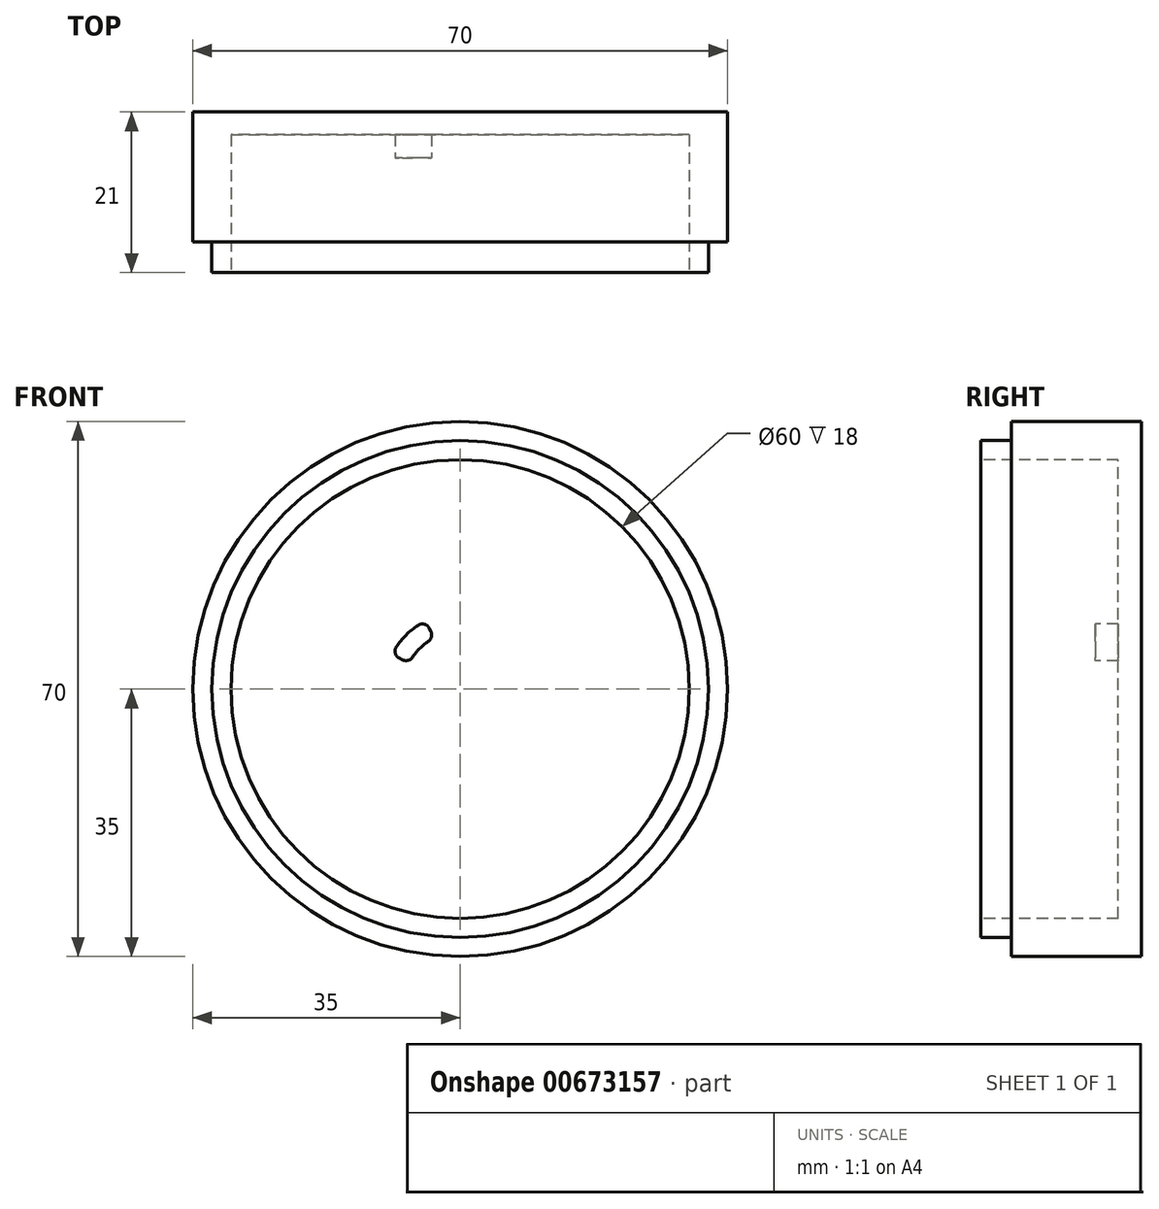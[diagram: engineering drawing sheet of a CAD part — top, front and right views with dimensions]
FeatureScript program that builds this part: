
annotation { "Feature Type Name" : "Feature", "Feature Type Description" : "" }
export const myFeature = defineFeature(function(context is Context, id is Id, definition is map)
    precondition{}
    {
        {
            var Q0;
            Q0=qCreatedBy(makeId("Front.planeOp"),FACE);
            var sketch = newSketch(context, id + "F0", { "sketchPlane" : qUnion([Q0])});
            skCircle(sketch, "E0", {"center": v(0, 0) * mm, "radius": 35 * mm});
            skSolve(sketch);
        }
        {
            var Q0;
            Q0=makeQuery(id+"F0.imprint","IMPRINT",FACE,{"disambiguationData":[TD([[makeQuery(id+"F0.imprint","IMPRINT",EDGE,{"derivedFrom":sQuery(id+"F0.wireOp",EDGE,"E0")}),1.0]])]});
            extrude(context, id + "F1", {"entities" : qUnion([Q0]), "depth" : 21 * mm, "offsetDistance" : 25 * mm});
        }
        {
            var Q0;
            Q0=makeQuery(id+"F1.opExtrude","CAP_FACE",FACE,{"disambiguationData":[OSD([sQuery(id+"F0.wireOp",EDGE,"E0")])],"isStart":false});
            var sketch = newSketch(context, id + "F2", { "sketchPlane" : qUnion([Q0])});
            skCircle(sketch, "E1", {"center": v(0, 0) * mm, "radius": 30 * mm});
            skSolve(sketch);
        }
        {
            var Q0;
            Q0=makeQuery(id+"F2.imprint","IMPRINT",FACE,{"disambiguationData":[TD([[makeQuery(id+"F2.imprint","IMPRINT",EDGE,{"derivedFrom":sQuery(id+"F2.wireOp",EDGE,"E1")}),1.0]])]});
            extrude(context, id + "F3", {"entities" : qUnion([Q0]), "operationType" : NewBodyOperationType.REMOVE, "oppositeDirection" : true, "depth" : 15 * mm, "offsetDistance" : 25 * mm});
        }
        {
            var Q0;
            Q0=makeQuery(id+"F1.opExtrude","CAP_FACE",FACE,{"disambiguationData":[OSD([sQuery(id+"F0.wireOp",EDGE,"E0")])],"isStart":false});
            var sketch = newSketch(context, id + "F4", { "sketchPlane" : qUnion([Q0])});
            skCircle(sketch, "E2", {"center": v(0, 0) * mm, "radius": 32.5 * mm});
            skSolve(sketch);
        }
        {
            var Q0;
            Q0=makeQuery(id+"F4.imprint","IMPRINT",FACE,{"disambiguationData":[TD([[makeQuery(id+"F4.imprint","IMPRINT",EDGE,{"derivedFrom":sQuery(id+"F4.wireOp",EDGE,"E2")}),-1.0]])]});
            extrude(context, id + "F5", {"entities" : qUnion([Q0]), "operationType" : NewBodyOperationType.REMOVE, "oppositeDirection" : true, "depth" : 4 * mm, "offsetDistance" : 25 * mm});
        }
        {
            var Q0;
            Q0=makeQuery(id+"F3.boolean.opBoolean","COPY",FACE,{"derivedFrom":makeQuery(id+"F3.opExtrude","CAP_FACE",FACE,{"disambiguationData":[OSD([sQuery(id+"F2.wireOp",EDGE,"E1")])],"isStart":false})});
            var sketch = newSketch(context, id + "F6", { "sketchPlane" : qUnion([Q0])});
            skLineSegment(sketch, "E3", {"start": v(0, 0) * mm, "end": v(0, 30) * mm, "construction": true});
            skLineSegment(sketch, "E4", {"start": v(-30, 0) * mm, "end": v(0, 0) * mm, "construction": true});
            skLineSegment(sketch, "E5", {"start": v(-2, 4) * mm, "end": v(-2, 25) * mm});
            skLineSegment(sketch, "E6", {"start": v(0, 27) * mm, "end": v(0, 27) * mm});
            skPoint(sketch, "E7.visualSharp", {"position": v(-2, 27) * mm});
            skArc(sketch, "E7.filletArc", {"start": v(0, 27) * mm, "mid": v(-1.41, 26.41) * mm, "end": v(-2, 25) * mm});
            skArc(sketch, "E8.MirrorCS", {"start": v(0, 27) * mm, "mid": v(1.41, 26.41) * mm, "end": v(2, 25) * mm});
            skLineSegment(sketch, "E9.MirrorCS", {"start": v(2, 4) * mm, "end": v(2, 25) * mm});
            skPoint(sketch, "E10.1.0", {"position": v(-27, -2) * mm});
            skLineSegment(sketch, "E10.1.1", {"start": v(-4, -2) * mm, "end": v(-25, -2) * mm});
            skLineSegment(sketch, "E10.1.2", {"start": v(-4, 2) * mm, "end": v(-25, 2) * mm});
            skArc(sketch, "E10.1.3", {"start": v(-27, 0) * mm, "mid": v(-26.41, -1.41) * mm, "end": v(-25, -2) * mm});
            skArc(sketch, "E10.1.4", {"start": v(-27, 0) * mm, "mid": v(-26.41, 1.41) * mm, "end": v(-25, 2) * mm});
            skPoint(sketch, "E10.2.0", {"position": v(2, -27) * mm});
            skLineSegment(sketch, "E10.2.1", {"start": v(2, -4) * mm, "end": v(2, -25) * mm});
            skLineSegment(sketch, "E10.2.2", {"start": v(-2, -4) * mm, "end": v(-2, -25) * mm});
            skArc(sketch, "E10.2.3", {"start": v(0, -27) * mm, "mid": v(1.41, -26.41) * mm, "end": v(2, -25) * mm});
            skArc(sketch, "E10.2.4", {"start": v(0, -27) * mm, "mid": v(-1.41, -26.41) * mm, "end": v(-2, -25) * mm});
            skPoint(sketch, "E10.3.0", {"position": v(27, 2) * mm});
            skLineSegment(sketch, "E10.3.1", {"start": v(4, 2) * mm, "end": v(25, 2) * mm});
            skLineSegment(sketch, "E10.3.2", {"start": v(4, -2) * mm, "end": v(25, -2) * mm});
            skArc(sketch, "E10.3.3", {"start": v(27, 0) * mm, "mid": v(26.41, 1.41) * mm, "end": v(25, 2) * mm});
            skArc(sketch, "E10.3.4", {"start": v(27, 0) * mm, "mid": v(26.41, -1.41) * mm, "end": v(25, -2) * mm});
            skPoint(sketch, "E10.center", {"position": v(0, 0) * mm});
            skPoint(sketch, "E11.orphan", {"position": v(0, 2) * mm});
            skPoint(sketch, "E12.orphan", {"position": v(0, -2) * mm});
            skPoint(sketch, "E13.orphan", {"position": v(-2, 0) * mm});
            skPoint(sketch, "E14.orphan", {"position": v(2, 0) * mm});
            skPoint(sketch, "E15.visualSharp", {"position": v(-2, 2) * mm});
            skArc(sketch, "E15.filletArc", {"start": v(-4, 2) * mm, "mid": v(-2.59, 2.59) * mm, "end": v(-2, 4) * mm});
            skPoint(sketch, "E16.visualSharp", {"position": v(2, 2) * mm});
            skArc(sketch, "E16.filletArc", {"start": v(2, 4) * mm, "mid": v(2.59, 2.59) * mm, "end": v(4, 2) * mm});
            skPoint(sketch, "E17.visualSharp", {"position": v(-2, -2) * mm});
            skArc(sketch, "E17.filletArc", {"start": v(-2, -4) * mm, "mid": v(-2.59, -2.59) * mm, "end": v(-4, -2) * mm});
            skPoint(sketch, "E18.visualSharp", {"position": v(2, -2) * mm});
            skArc(sketch, "E18.filletArc", {"start": v(4, -2) * mm, "mid": v(2.59, -2.59) * mm, "end": v(2, -4) * mm});
            skSolve(sketch);
        }
        {
            var Q0;
            Q0=makeQuery(id+"F6.imprint","IMPRINT",FACE,{"disambiguationData":[TD([[makeQuery(id+"F6.imprint","IMPRINT",EDGE,{"derivedFrom":sQuery(id+"F6.wireOp",EDGE,"E5")}),-1.0]])]});
            extrude(context, id + "F7", {"entities" : qUnion([Q0]), "operationType" : NewBodyOperationType.REMOVE, "oppositeDirection" : true, "depth" : 3 * mm, "offsetDistance" : 25 * mm});
        }
        {
            var Q0;
            Q0=makeQuery(id+"F3.boolean.opBoolean","COPY",FACE,{"derivedFrom":makeQuery(id+"F3.opExtrude","CAP_FACE",FACE,{"disambiguationData":[OSD([sQuery(id+"F2.wireOp",EDGE,"E1")])],"isStart":false})});
            var sketch = newSketch(context, id + "F8", { "sketchPlane" : qUnion([Q0])});
            skLineSegment(sketch, "E19", {"start": v(0, 0) * mm, "end": v(-21.21, 21.21) * mm, "construction": true});
            skArc(sketch, "E20", {"start": v(-5.3, 5.3) * mm, "mid": v(-4.75, 5.8) * mm, "end": v(-4.16, 6.24) * mm});
            skLineSegment(sketch, "E21", {"start": v(-3.82, 7.53) * mm, "end": v(-4.05, 7.98) * mm});
            skArc(sketch, "E22", {"start": v(-7.07, 7.07) * mm, "mid": v(-6.31, 7.76) * mm, "end": v(-5.49, 8.36) * mm});
            skArc(sketch, "E23.filletArc", {"start": v(-4.05, 7.98) * mm, "mid": v(-4.68, 8.49) * mm, "end": v(-5.49, 8.36) * mm});
            skArc(sketch, "E24.filletArc", {"start": v(-4.16, 6.24) * mm, "mid": v(-3.75, 6.82) * mm, "end": v(-3.82, 7.53) * mm});
            skArc(sketch, "E25.MirrorCS", {"start": v(-7.07, 7.07) * mm, "mid": v(-7.76, 6.31) * mm, "end": v(-8.36, 5.49) * mm});
            skArc(sketch, "E26.MirrorCS", {"start": v(-7.98, 4.05) * mm, "mid": v(-8.49, 4.68) * mm, "end": v(-8.36, 5.49) * mm});
            skArc(sketch, "E27.MirrorCS", {"start": v(-6.24, 4.16) * mm, "mid": v(-6.82, 3.75) * mm, "end": v(-7.53, 3.82) * mm});
            skArc(sketch, "E28.MirrorCS", {"start": v(-5.3, 5.3) * mm, "mid": v(-5.8, 4.75) * mm, "end": v(-6.24, 4.16) * mm});
            skLineSegment(sketch, "E29.MirrorCS", {"start": v(-7.53, 3.82) * mm, "end": v(-7.98, 4.05) * mm});
            skLineSegment(sketch, "E30.1.0", {"start": v(-7.53, -3.82) * mm, "end": v(-7.98, -4.05) * mm});
            skLineSegment(sketch, "E30.1.1", {"start": v(-3.82, -7.53) * mm, "end": v(-4.05, -7.98) * mm});
            skArc(sketch, "E30.1.2", {"start": v(-5.3, -5.3) * mm, "mid": v(-4.75, -5.8) * mm, "end": v(-4.16, -6.24) * mm});
            skArc(sketch, "E30.1.3", {"start": v(-4.16, -6.24) * mm, "mid": v(-3.75, -6.82) * mm, "end": v(-3.82, -7.53) * mm});
            skArc(sketch, "E30.1.4", {"start": v(-4.05, -7.98) * mm, "mid": v(-4.68, -8.49) * mm, "end": v(-5.49, -8.36) * mm});
            skArc(sketch, "E30.1.5", {"start": v(-7.07, -7.07) * mm, "mid": v(-6.31, -7.76) * mm, "end": v(-5.49, -8.36) * mm});
            skArc(sketch, "E30.1.6", {"start": v(-7.07, -7.07) * mm, "mid": v(-7.76, -6.31) * mm, "end": v(-8.36, -5.49) * mm});
            skArc(sketch, "E30.1.7", {"start": v(-5.3, -5.3) * mm, "mid": v(-5.8, -4.75) * mm, "end": v(-6.24, -4.16) * mm});
            skArc(sketch, "E30.1.8", {"start": v(-6.24, -4.16) * mm, "mid": v(-6.82, -3.75) * mm, "end": v(-7.53, -3.82) * mm});
            skArc(sketch, "E30.1.9", {"start": v(-7.98, -4.05) * mm, "mid": v(-8.49, -4.68) * mm, "end": v(-8.36, -5.49) * mm});
            skLineSegment(sketch, "E30.2.0", {"start": v(3.82, -7.53) * mm, "end": v(4.05, -7.98) * mm});
            skLineSegment(sketch, "E30.2.1", {"start": v(7.53, -3.82) * mm, "end": v(7.98, -4.05) * mm});
            skArc(sketch, "E30.2.2", {"start": v(5.3, -5.3) * mm, "mid": v(5.8, -4.75) * mm, "end": v(6.24, -4.16) * mm});
            skArc(sketch, "E30.2.3", {"start": v(6.24, -4.16) * mm, "mid": v(6.82, -3.75) * mm, "end": v(7.53, -3.82) * mm});
            skArc(sketch, "E30.2.4", {"start": v(7.98, -4.05) * mm, "mid": v(8.49, -4.68) * mm, "end": v(8.36, -5.49) * mm});
            skArc(sketch, "E30.2.5", {"start": v(7.07, -7.07) * mm, "mid": v(7.76, -6.31) * mm, "end": v(8.36, -5.49) * mm});
            skArc(sketch, "E30.2.6", {"start": v(7.07, -7.07) * mm, "mid": v(6.31, -7.76) * mm, "end": v(5.49, -8.36) * mm});
            skArc(sketch, "E30.2.7", {"start": v(5.3, -5.3) * mm, "mid": v(4.75, -5.8) * mm, "end": v(4.16, -6.24) * mm});
            skArc(sketch, "E30.2.8", {"start": v(4.16, -6.24) * mm, "mid": v(3.75, -6.82) * mm, "end": v(3.82, -7.53) * mm});
            skArc(sketch, "E30.2.9", {"start": v(4.05, -7.98) * mm, "mid": v(4.68, -8.49) * mm, "end": v(5.49, -8.36) * mm});
            skLineSegment(sketch, "E30.3.0", {"start": v(7.53, 3.82) * mm, "end": v(7.98, 4.05) * mm});
            skLineSegment(sketch, "E30.3.1", {"start": v(3.82, 7.53) * mm, "end": v(4.05, 7.98) * mm});
            skArc(sketch, "E30.3.2", {"start": v(5.3, 5.3) * mm, "mid": v(4.75, 5.8) * mm, "end": v(4.16, 6.24) * mm});
            skArc(sketch, "E30.3.3", {"start": v(4.16, 6.24) * mm, "mid": v(3.75, 6.82) * mm, "end": v(3.82, 7.53) * mm});
            skArc(sketch, "E30.3.4", {"start": v(4.05, 7.98) * mm, "mid": v(4.68, 8.49) * mm, "end": v(5.49, 8.36) * mm});
            skArc(sketch, "E30.3.5", {"start": v(7.07, 7.07) * mm, "mid": v(6.31, 7.76) * mm, "end": v(5.49, 8.36) * mm});
            skArc(sketch, "E30.3.6", {"start": v(7.07, 7.07) * mm, "mid": v(7.76, 6.31) * mm, "end": v(8.36, 5.49) * mm});
            skArc(sketch, "E30.3.7", {"start": v(5.3, 5.3) * mm, "mid": v(5.8, 4.75) * mm, "end": v(6.24, 4.16) * mm});
            skArc(sketch, "E30.3.8", {"start": v(6.24, 4.16) * mm, "mid": v(6.82, 3.75) * mm, "end": v(7.53, 3.82) * mm});
            skArc(sketch, "E30.3.9", {"start": v(7.98, 4.05) * mm, "mid": v(8.49, 4.68) * mm, "end": v(8.36, 5.49) * mm});
            skSolve(sketch);
        }
        {
            var Q0;
            Q0=makeQuery(id+"F8.imprint","IMPRINT",FACE,{"disambiguationData":[TD([[makeQuery(id+"F8.imprint","IMPRINT",EDGE,{"derivedFrom":sQuery(id+"F8.wireOp",EDGE,"E20")}),1.0]])]});
            var Q1;
            Q1=makeQuery(id+"F8.imprint","IMPRINT",FACE,{"disambiguationData":[TD([[makeQuery(id+"F8.imprint","IMPRINT",EDGE,{"derivedFrom":sQuery(id+"F8.wireOp",EDGE,"E30.3.0")}),1.0]])]});
            var Q2;
            Q2=makeQuery(id+"F8.imprint","IMPRINT",FACE,{"disambiguationData":[TD([[makeQuery(id+"F8.imprint","IMPRINT",EDGE,{"derivedFrom":sQuery(id+"F8.wireOp",EDGE,"E30.2.0")}),1.0]])]});
            var Q3;
            Q3=makeQuery(id+"F8.imprint","IMPRINT",FACE,{"disambiguationData":[TD([[makeQuery(id+"F8.imprint","IMPRINT",EDGE,{"derivedFrom":sQuery(id+"F8.wireOp",EDGE,"E30.1.0")}),1.0]])]});
            extrude(context, id + "F9", {"entities" : qUnion([Q0, Q1, Q2, Q3]), "operationType" : NewBodyOperationType.REMOVE, "oppositeDirection" : true, "depth" : 3 * mm, "offsetDistance" : 25 * mm});
        }
        {
            var Q0;
            Q0=makeQuery(id+"F3.boolean.opBoolean","COPY",FACE,{"derivedFrom":makeQuery(id+"F3.opExtrude","CAP_FACE",FACE,{"disambiguationData":[OSD([sQuery(id+"F2.wireOp",EDGE,"E1")])],"isStart":false})});
            var sketch = newSketch(context, id + "F10", { "sketchPlane" : qUnion([Q0])});
            skLineSegment(sketch, "E31", {"start": v(-9.93, 11.83) * mm, "end": v(-10.58, 12.6) * mm});
            skLineSegment(sketch, "E32", {"start": v(-3.82, 14.06) * mm, "end": v(-3.82, 15.06) * mm});
            skArc(sketch, "E33", {"start": v(-9.04, 10.77) * mm, "mid": v(-10.1, 9.8) * mm, "end": v(-11.04, 8.71) * mm, "construction": true});
            skArc(sketch, "E34", {"start": v(-8, 11.51) * mm, "mid": v(-6.6, 12.19) * mm, "end": v(-5.09, 12.58) * mm});
            skArc(sketch, "E35", {"start": v(-10.22, 14.84) * mm, "mid": v(-7.96, 15.94) * mm, "end": v(-5.53, 16.55) * mm});
            skArc(sketch, "E36.filletArc", {"start": v(-3.82, 15.06) * mm, "mid": v(-4.34, 16.2) * mm, "end": v(-5.53, 16.55) * mm});
            skPoint(sketch, "E37.newPointA", {"position": v(-3.82, 0) * mm});
            skArc(sketch, "E37.filletArc", {"start": v(-5.09, 12.58) * mm, "mid": v(-4.18, 13.08) * mm, "end": v(-3.82, 14.06) * mm});
            skArc(sketch, "E38.filletArc", {"start": v(-10.22, 14.84) * mm, "mid": v(-10.9, 13.8) * mm, "end": v(-10.58, 12.6) * mm});
            skArc(sketch, "E39.filletArc", {"start": v(-9.93, 11.83) * mm, "mid": v(-9.03, 11.32) * mm, "end": v(-8, 11.51) * mm});
            skLineSegment(sketch, "E40", {"start": v(-3.82, 4.55) * mm, "end": v(0, 0) * mm, "construction": true});
            skLineSegment(sketch, "E41", {"start": v(0, 0) * mm, "end": v(-21.21, 21.21) * mm, "construction": true});
            skArc(sketch, "E42.MirrorCS", {"start": v(-15.06, 3.82) * mm, "mid": v(-16.2, 4.34) * mm, "end": v(-16.55, 5.53) * mm});
            skLineSegment(sketch, "E43.MirrorCS", {"start": v(-14.06, 3.82) * mm, "end": v(-15.06, 3.82) * mm});
            skArc(sketch, "E44.MirrorCS", {"start": v(-12.58, 5.09) * mm, "mid": v(-13.08, 4.18) * mm, "end": v(-14.06, 3.82) * mm});
            skArc(sketch, "E45.MirrorCS", {"start": v(-11.51, 8) * mm, "mid": v(-12.19, 6.6) * mm, "end": v(-12.58, 5.09) * mm});
            skArc(sketch, "E46.MirrorCS", {"start": v(-11.83, 9.93) * mm, "mid": v(-11.32, 9.03) * mm, "end": v(-11.51, 8) * mm});
            skLineSegment(sketch, "E47.MirrorCS", {"start": v(-11.83, 9.93) * mm, "end": v(-12.6, 10.58) * mm});
            skArc(sketch, "E48.MirrorCS", {"start": v(-14.84, 10.22) * mm, "mid": v(-13.8, 10.9) * mm, "end": v(-12.6, 10.58) * mm});
            skArc(sketch, "E49.MirrorCS", {"start": v(-14.84, 10.22) * mm, "mid": v(-15.94, 7.96) * mm, "end": v(-16.55, 5.53) * mm});
            skLineSegment(sketch, "E50", {"start": v(0, 0) * mm, "end": v(-30, 0) * mm, "construction": true});
            skLineSegment(sketch, "E51.MirrorCS", {"start": v(-9.93, -11.83) * mm, "end": v(-10.58, -12.6) * mm});
            skLineSegment(sketch, "E52.MirrorCS", {"start": v(-3.82, -14.06) * mm, "end": v(-3.82, -15.06) * mm});
            skLineSegment(sketch, "E53.MirrorCS", {"start": v(-11.83, -9.93) * mm, "end": v(-12.6, -10.58) * mm});
            skLineSegment(sketch, "E54.MirrorCS", {"start": v(-14.06, -3.82) * mm, "end": v(-15.06, -3.82) * mm});
            skArc(sketch, "E55.MirrorCS", {"start": v(-11.51, -8) * mm, "mid": v(-12.19, -6.6) * mm, "end": v(-12.58, -5.09) * mm});
            skArc(sketch, "E56.MirrorCS", {"start": v(-11.83, -9.93) * mm, "mid": v(-11.32, -9.03) * mm, "end": v(-11.51, -8) * mm});
            skArc(sketch, "E57.MirrorCS", {"start": v(-12.58, -5.09) * mm, "mid": v(-13.08, -4.18) * mm, "end": v(-14.06, -3.82) * mm});
            skArc(sketch, "E58.MirrorCS", {"start": v(-15.06, -3.82) * mm, "mid": v(-16.2, -4.34) * mm, "end": v(-16.55, -5.53) * mm});
            skArc(sketch, "E59.MirrorCS", {"start": v(-14.84, -10.22) * mm, "mid": v(-13.8, -10.9) * mm, "end": v(-12.6, -10.58) * mm});
            skArc(sketch, "E60.MirrorCS", {"start": v(-5.09, -12.58) * mm, "mid": v(-4.18, -13.08) * mm, "end": v(-3.82, -14.06) * mm});
            skArc(sketch, "E61.MirrorCS", {"start": v(-10.22, -14.84) * mm, "mid": v(-10.9, -13.8) * mm, "end": v(-10.58, -12.6) * mm});
            skArc(sketch, "E62.MirrorCS", {"start": v(-9.93, -11.83) * mm, "mid": v(-9.03, -11.32) * mm, "end": v(-8, -11.51) * mm});
            skArc(sketch, "E63.MirrorCS", {"start": v(-9.04, -10.77) * mm, "mid": v(-10.1, -9.8) * mm, "end": v(-11.04, -8.71) * mm, "construction": true});
            skArc(sketch, "E64.MirrorCS", {"start": v(-8, -11.51) * mm, "mid": v(-6.6, -12.19) * mm, "end": v(-5.09, -12.58) * mm});
            skArc(sketch, "E65.MirrorCS", {"start": v(-14.84, -10.22) * mm, "mid": v(-15.94, -7.96) * mm, "end": v(-16.55, -5.53) * mm});
            skArc(sketch, "E66.MirrorCS", {"start": v(-3.82, -15.06) * mm, "mid": v(-4.34, -16.2) * mm, "end": v(-5.53, -16.55) * mm});
            skArc(sketch, "E67.MirrorCS", {"start": v(-10.22, -14.84) * mm, "mid": v(-7.96, -15.94) * mm, "end": v(-5.53, -16.55) * mm});
            skLineSegment(sketch, "E68", {"start": v(0, 0) * mm, "end": v(0, 27) * mm, "construction": true});
            skLineSegment(sketch, "E69.MirrorCS", {"start": v(9.93, -11.83) * mm, "end": v(10.58, -12.6) * mm});
            skArc(sketch, "E70.MirrorCS", {"start": v(9.93, -11.83) * mm, "mid": v(9.03, -11.32) * mm, "end": v(8, -11.51) * mm});
            skLineSegment(sketch, "E71.MirrorCS", {"start": v(3.82, -14.06) * mm, "end": v(3.82, -15.06) * mm});
            skArc(sketch, "E72.MirrorCS", {"start": v(11.83, -9.93) * mm, "mid": v(11.32, -9.03) * mm, "end": v(11.51, -8) * mm});
            skLineSegment(sketch, "E73.MirrorCS", {"start": v(11.83, 9.93) * mm, "end": v(12.6, 10.58) * mm});
            skLineSegment(sketch, "E74.MirrorCS", {"start": v(11.83, -9.93) * mm, "end": v(12.6, -10.58) * mm});
            skLineSegment(sketch, "E75.MirrorCS", {"start": v(14.06, 3.82) * mm, "end": v(15.06, 3.82) * mm});
            skLineSegment(sketch, "E76.MirrorCS", {"start": v(14.06, -3.82) * mm, "end": v(15.06, -3.82) * mm});
            skArc(sketch, "E77.MirrorCS", {"start": v(9.93, 11.83) * mm, "mid": v(9.03, 11.32) * mm, "end": v(8, 11.51) * mm});
            skArc(sketch, "E78.MirrorCS", {"start": v(11.83, 9.93) * mm, "mid": v(11.32, 9.03) * mm, "end": v(11.51, 8) * mm});
            skLineSegment(sketch, "E79.MirrorCS", {"start": v(3.82, 14.06) * mm, "end": v(3.82, 15.06) * mm});
            skLineSegment(sketch, "E80.MirrorCS", {"start": v(9.93, 11.83) * mm, "end": v(10.58, 12.6) * mm});
            skArc(sketch, "E81.MirrorCS", {"start": v(12.58, 5.09) * mm, "mid": v(13.08, 4.18) * mm, "end": v(14.06, 3.82) * mm});
            skArc(sketch, "E82.MirrorCS", {"start": v(5.09, -12.58) * mm, "mid": v(4.18, -13.08) * mm, "end": v(3.82, -14.06) * mm});
            skArc(sketch, "E83.MirrorCS", {"start": v(10.22, -14.84) * mm, "mid": v(10.9, -13.8) * mm, "end": v(10.58, -12.6) * mm});
            skArc(sketch, "E84.MirrorCS", {"start": v(8, -11.51) * mm, "mid": v(6.6, -12.19) * mm, "end": v(5.09, -12.58) * mm});
            skArc(sketch, "E85.MirrorCS", {"start": v(10.22, 14.84) * mm, "mid": v(10.9, 13.8) * mm, "end": v(10.58, 12.6) * mm});
            skArc(sketch, "E86.MirrorCS", {"start": v(12.58, -5.09) * mm, "mid": v(13.08, -4.18) * mm, "end": v(14.06, -3.82) * mm});
            skArc(sketch, "E87.MirrorCS", {"start": v(15.06, -3.82) * mm, "mid": v(16.2, -4.34) * mm, "end": v(16.55, -5.53) * mm});
            skArc(sketch, "E88.MirrorCS", {"start": v(10.22, -14.84) * mm, "mid": v(7.96, -15.94) * mm, "end": v(5.53, -16.55) * mm});
            skArc(sketch, "E89.MirrorCS", {"start": v(9.04, -10.77) * mm, "mid": v(10.1, -9.8) * mm, "end": v(11.04, -8.71) * mm, "construction": true});
            skArc(sketch, "E90.MirrorCS", {"start": v(3.82, -15.06) * mm, "mid": v(4.34, -16.2) * mm, "end": v(5.53, -16.55) * mm});
            skArc(sketch, "E91.MirrorCS", {"start": v(15.06, 3.82) * mm, "mid": v(16.2, 4.34) * mm, "end": v(16.55, 5.53) * mm});
            skArc(sketch, "E92.MirrorCS", {"start": v(14.84, -10.22) * mm, "mid": v(13.8, -10.9) * mm, "end": v(12.6, -10.58) * mm});
            skArc(sketch, "E93.MirrorCS", {"start": v(14.84, 10.22) * mm, "mid": v(13.8, 10.9) * mm, "end": v(12.6, 10.58) * mm});
            skArc(sketch, "E94.MirrorCS", {"start": v(5.09, 12.58) * mm, "mid": v(4.18, 13.08) * mm, "end": v(3.82, 14.06) * mm});
            skArc(sketch, "E95.MirrorCS", {"start": v(9.04, 10.77) * mm, "mid": v(10.1, 9.8) * mm, "end": v(11.04, 8.71) * mm, "construction": true});
            skArc(sketch, "E96.MirrorCS", {"start": v(14.84, 10.22) * mm, "mid": v(15.94, 7.96) * mm, "end": v(16.55, 5.53) * mm});
            skArc(sketch, "E97.MirrorCS", {"start": v(14.84, -10.22) * mm, "mid": v(15.94, -7.96) * mm, "end": v(16.55, -5.53) * mm});
            skArc(sketch, "E98.MirrorCS", {"start": v(8, 11.51) * mm, "mid": v(6.6, 12.19) * mm, "end": v(5.09, 12.58) * mm});
            skArc(sketch, "E99.MirrorCS", {"start": v(11.51, -8) * mm, "mid": v(12.19, -6.6) * mm, "end": v(12.58, -5.09) * mm});
            skArc(sketch, "E100.MirrorCS", {"start": v(11.51, 8) * mm, "mid": v(12.19, 6.6) * mm, "end": v(12.58, 5.09) * mm});
            skPoint(sketch, "E101.MirrorP", {"position": v(3.82, 0) * mm});
            skArc(sketch, "E102.MirrorCS", {"start": v(3.82, 15.06) * mm, "mid": v(4.34, 16.2) * mm, "end": v(5.53, 16.55) * mm});
            skArc(sketch, "E103.MirrorCS", {"start": v(10.22, 14.84) * mm, "mid": v(7.96, 15.94) * mm, "end": v(5.53, 16.55) * mm});
            skSolve(sketch);
        }
        {
            var Q0;
            Q0=makeQuery(id+"F10.imprint","IMPRINT",FACE,{"disambiguationData":[TD([[makeQuery(id+"F10.imprint","IMPRINT",EDGE,{"derivedFrom":sQuery(id+"F10.wireOp",EDGE,"E31")}),-1.0]])]});
            var Q1;
            Q1=makeQuery(id+"F10.imprint","IMPRINT",FACE,{"disambiguationData":[TD([[makeQuery(id+"F10.imprint","IMPRINT",EDGE,{"derivedFrom":sQuery(id+"F10.wireOp",EDGE,"E42.MirrorCS")}),-1.0]])]});
            var Q2;
            Q2=makeQuery(id+"F10.imprint","IMPRINT",FACE,{"disambiguationData":[TD([[makeQuery(id+"F10.imprint","IMPRINT",EDGE,{"derivedFrom":sQuery(id+"F10.wireOp",EDGE,"E53.MirrorCS")}),-1.0]])]});
            var Q3;
            Q3=makeQuery(id+"F10.imprint","IMPRINT",FACE,{"disambiguationData":[TD([[makeQuery(id+"F10.imprint","IMPRINT",EDGE,{"derivedFrom":sQuery(id+"F10.wireOp",EDGE,"E62.MirrorCS")}),-1.0]])]});
            var Q4;
            Q4=makeQuery(id+"F10.imprint","IMPRINT",FACE,{"disambiguationData":[TD([[makeQuery(id+"F10.imprint","IMPRINT",EDGE,{"derivedFrom":sQuery(id+"F10.wireOp",EDGE,"E72.MirrorCS")}),-1.0]])]});
            var Q5;
            Q5=makeQuery(id+"F10.imprint","IMPRINT",FACE,{"disambiguationData":[TD([[makeQuery(id+"F10.imprint","IMPRINT",EDGE,{"derivedFrom":sQuery(id+"F10.wireOp",EDGE,"E73.MirrorCS")}),-1.0]])]});
            var Q6;
            Q6=makeQuery(id+"F10.imprint","IMPRINT",FACE,{"disambiguationData":[TD([[makeQuery(id+"F10.imprint","IMPRINT",EDGE,{"derivedFrom":sQuery(id+"F10.wireOp",EDGE,"E77.MirrorCS")}),-1.0]])]});
            var Q7;
            Q7=makeQuery(id+"F10.imprint","IMPRINT",FACE,{"disambiguationData":[TD([[makeQuery(id+"F10.imprint","IMPRINT",EDGE,{"derivedFrom":sQuery(id+"F10.wireOp",EDGE,"E70.MirrorCS")}),1.0]])]});
            extrude(context, id + "F11", {"entities" : qUnion([Q0, Q1, Q2, Q3, Q4, Q5, Q6, Q7]), "operationType" : NewBodyOperationType.REMOVE, "oppositeDirection" : true, "depth" : 3 * mm, "offsetDistance" : 25 * mm});
        }
        {
            var Q0;
            Q0=makeQuery(id+"F3.boolean.opBoolean","COPY",FACE,{"derivedFrom":makeQuery(id+"F3.opExtrude","CAP_FACE",FACE,{"disambiguationData":[OSD([sQuery(id+"F2.wireOp",EDGE,"E1")])],"isStart":false})});
            var sketch = newSketch(context, id + "F12", { "sketchPlane" : qUnion([Q0])});
            skLineSegment(sketch, "E104", {"start": v(-14.1, 16.8) * mm, "end": v(-15.66, 18.67) * mm});
            skLineSegment(sketch, "E105", {"start": v(-3.82, 20.55) * mm, "end": v(-3.82, 22.98) * mm});
            skArc(sketch, "E106", {"start": v(-13.17, 15.7) * mm, "mid": v(-14.87, 14.12) * mm, "end": v(-16.4, 12.37) * mm, "construction": true});
            skArc(sketch, "E107", {"start": v(-12.1, 16.54) * mm, "mid": v(-8.8, 18.24) * mm, "end": v(-5.18, 19.05) * mm});
            skArc(sketch, "E108", {"start": v(-15.38, 20.86) * mm, "mid": v(-10.66, 23.33) * mm, "end": v(-5.44, 24.47) * mm});
            skArc(sketch, "E109.filletArc", {"start": v(-15.38, 20.86) * mm, "mid": v(-16, 19.82) * mm, "end": v(-15.66, 18.67) * mm});
            skArc(sketch, "E110.filletArc", {"start": v(-14.1, 16.8) * mm, "mid": v(-13.15, 16.28) * mm, "end": v(-12.1, 16.54) * mm});
            skArc(sketch, "E111.filletArc", {"start": v(-3.82, 22.98) * mm, "mid": v(-4.3, 24.08) * mm, "end": v(-5.44, 24.47) * mm});
            skPoint(sketch, "E112.newPointA", {"position": v(-3.82, 0) * mm});
            skArc(sketch, "E112.filletArc", {"start": v(-5.18, 19.05) * mm, "mid": v(-4.21, 19.54) * mm, "end": v(-3.82, 20.55) * mm});
            skLineSegment(sketch, "E113", {"start": v(-0.17, -0.18) * mm, "end": v(-21.39, 21.04) * mm, "construction": true});
            skLineSegment(sketch, "E114.MirrorCS", {"start": v(-17.16, 13.75) * mm, "end": v(-19.02, 15.31) * mm});
            skLineSegment(sketch, "E115.MirrorCS", {"start": v(-20.9, 3.47) * mm, "end": v(-23.33, 3.47) * mm});
            skArc(sketch, "E116.MirrorCS", {"start": v(-16.89, 11.75) * mm, "mid": v(-18.6, 8.45) * mm, "end": v(-19.4, 4.83) * mm});
            skArc(sketch, "E117.MirrorCS", {"start": v(-21.2, 15.03) * mm, "mid": v(-20.18, 15.65) * mm, "end": v(-19.02, 15.31) * mm});
            skArc(sketch, "E118.MirrorCS", {"start": v(-17.16, 13.75) * mm, "mid": v(-16.63, 12.8) * mm, "end": v(-16.89, 11.75) * mm});
            skArc(sketch, "E119.MirrorCS", {"start": v(-19.4, 4.83) * mm, "mid": v(-19.89, 3.86) * mm, "end": v(-20.9, 3.47) * mm});
            skArc(sketch, "E120.MirrorCS", {"start": v(-21.2, 15.03) * mm, "mid": v(-23.69, 10.3) * mm, "end": v(-24.83, 5.1) * mm});
            skArc(sketch, "E121.MirrorCS", {"start": v(-23.33, 3.47) * mm, "mid": v(-24.43, 3.95) * mm, "end": v(-24.83, 5.1) * mm});
            skLineSegment(sketch, "E122", {"start": v(0, 0) * mm, "end": v(-30, 0) * mm, "construction": true});
            skPoint(sketch, "E122.endSnap0", {"position": v(-27, 0) * mm});
            skArc(sketch, "E123.MirrorCS", {"start": v(-17.16, -13.75) * mm, "mid": v(-16.63, -12.8) * mm, "end": v(-16.89, -11.75) * mm});
            skArc(sketch, "E124.MirrorCS", {"start": v(-21.2, -15.03) * mm, "mid": v(-20.18, -15.65) * mm, "end": v(-19.02, -15.31) * mm});
            skArc(sketch, "E125.MirrorCS", {"start": v(-19.4, -4.83) * mm, "mid": v(-19.89, -3.86) * mm, "end": v(-20.9, -3.47) * mm});
            skLineSegment(sketch, "E126.MirrorCS", {"start": v(-14.1, -16.8) * mm, "end": v(-15.66, -18.67) * mm});
            skLineSegment(sketch, "E127.MirrorCS", {"start": v(-3.82, -20.55) * mm, "end": v(-3.82, -22.98) * mm});
            skArc(sketch, "E128.MirrorCS", {"start": v(-23.33, -3.47) * mm, "mid": v(-24.43, -3.95) * mm, "end": v(-24.83, -5.1) * mm});
            skArc(sketch, "E129.MirrorCS", {"start": v(-15.38, -20.86) * mm, "mid": v(-16, -19.82) * mm, "end": v(-15.66, -18.67) * mm});
            skArc(sketch, "E130.MirrorCS", {"start": v(-14.1, -16.8) * mm, "mid": v(-13.15, -16.28) * mm, "end": v(-12.1, -16.54) * mm});
            skArc(sketch, "E131.MirrorCS", {"start": v(-3.82, -22.98) * mm, "mid": v(-4.3, -24.08) * mm, "end": v(-5.44, -24.47) * mm});
            skArc(sketch, "E132.MirrorCS", {"start": v(-5.18, -19.05) * mm, "mid": v(-4.21, -19.54) * mm, "end": v(-3.82, -20.55) * mm});
            skLineSegment(sketch, "E133.MirrorCS", {"start": v(-17.16, -13.75) * mm, "end": v(-19.02, -15.31) * mm});
            skLineSegment(sketch, "E134.MirrorCS", {"start": v(-20.9, -3.47) * mm, "end": v(-23.33, -3.47) * mm});
            skArc(sketch, "E135.MirrorCS", {"start": v(-13.17, -15.7) * mm, "mid": v(-14.87, -14.12) * mm, "end": v(-16.4, -12.37) * mm, "construction": true});
            skArc(sketch, "E136.MirrorCS", {"start": v(-12.1, -16.54) * mm, "mid": v(-8.8, -18.24) * mm, "end": v(-5.18, -19.05) * mm});
            skArc(sketch, "E137.MirrorCS", {"start": v(-15.38, -20.86) * mm, "mid": v(-10.66, -23.33) * mm, "end": v(-5.44, -24.47) * mm});
            skArc(sketch, "E138.MirrorCS", {"start": v(-21.2, -15.03) * mm, "mid": v(-23.69, -10.3) * mm, "end": v(-24.83, -5.1) * mm});
            skArc(sketch, "E139.MirrorCS", {"start": v(-16.89, -11.75) * mm, "mid": v(-18.6, -8.45) * mm, "end": v(-19.4, -4.83) * mm});
            skLineSegment(sketch, "E140", {"start": v(0, 0) * mm, "end": v(0, -30) * mm, "construction": true});
            skLineSegment(sketch, "E141.MirrorCS", {"start": v(3.82, 20.55) * mm, "end": v(3.82, 22.98) * mm});
            skLineSegment(sketch, "E142.MirrorCS", {"start": v(3.82, -20.55) * mm, "end": v(3.82, -22.98) * mm});
            skArc(sketch, "E143.MirrorCS", {"start": v(23.33, 3.47) * mm, "mid": v(24.43, 3.95) * mm, "end": v(24.83, 5.1) * mm});
            skArc(sketch, "E144.MirrorCS", {"start": v(23.33, -3.47) * mm, "mid": v(24.43, -3.95) * mm, "end": v(24.83, -5.1) * mm});
            skArc(sketch, "E145.MirrorCS", {"start": v(15.38, -20.86) * mm, "mid": v(16, -19.82) * mm, "end": v(15.66, -18.67) * mm});
            skArc(sketch, "E146.MirrorCS", {"start": v(17.16, -13.75) * mm, "mid": v(16.63, -12.8) * mm, "end": v(16.89, -11.75) * mm});
            skArc(sketch, "E147.MirrorCS", {"start": v(14.1, -16.8) * mm, "mid": v(13.15, -16.28) * mm, "end": v(12.1, -16.54) * mm});
            skLineSegment(sketch, "E148.MirrorCS", {"start": v(17.16, -13.75) * mm, "end": v(19.02, -15.31) * mm});
            skArc(sketch, "E149.MirrorCS", {"start": v(21.2, -15.03) * mm, "mid": v(20.18, -15.65) * mm, "end": v(19.02, -15.31) * mm});
            skArc(sketch, "E150.MirrorCS", {"start": v(3.82, -22.98) * mm, "mid": v(4.3, -24.08) * mm, "end": v(5.44, -24.47) * mm});
            skArc(sketch, "E151.MirrorCS", {"start": v(14.1, 16.8) * mm, "mid": v(13.15, 16.28) * mm, "end": v(12.1, 16.54) * mm});
            skArc(sketch, "E152.MirrorCS", {"start": v(3.82, 22.98) * mm, "mid": v(4.3, 24.08) * mm, "end": v(5.44, 24.47) * mm});
            skArc(sketch, "E153.MirrorCS", {"start": v(21.2, 15.03) * mm, "mid": v(20.18, 15.65) * mm, "end": v(19.02, 15.31) * mm});
            skArc(sketch, "E154.MirrorCS", {"start": v(17.16, 13.75) * mm, "mid": v(16.63, 12.8) * mm, "end": v(16.89, 11.75) * mm});
            skArc(sketch, "E155.MirrorCS", {"start": v(5.18, 19.05) * mm, "mid": v(4.21, 19.54) * mm, "end": v(3.82, 20.55) * mm});
            skLineSegment(sketch, "E156.MirrorCS", {"start": v(17.16, 13.75) * mm, "end": v(19.02, 15.31) * mm});
            skLineSegment(sketch, "E157.MirrorCS", {"start": v(20.9, 3.47) * mm, "end": v(23.33, 3.47) * mm});
            skArc(sketch, "E158.MirrorCS", {"start": v(15.38, 20.86) * mm, "mid": v(16, 19.82) * mm, "end": v(15.66, 18.67) * mm});
            skArc(sketch, "E159.MirrorCS", {"start": v(19.4, 4.83) * mm, "mid": v(19.89, 3.86) * mm, "end": v(20.9, 3.47) * mm});
            skArc(sketch, "E160.MirrorCS", {"start": v(5.18, -19.05) * mm, "mid": v(4.21, -19.54) * mm, "end": v(3.82, -20.55) * mm});
            skLineSegment(sketch, "E161.MirrorCS", {"start": v(14.1, 16.8) * mm, "end": v(15.66, 18.67) * mm});
            skArc(sketch, "E162.MirrorCS", {"start": v(19.4, -4.83) * mm, "mid": v(19.89, -3.86) * mm, "end": v(20.9, -3.47) * mm});
            skLineSegment(sketch, "E163.MirrorCS", {"start": v(14.1, -16.8) * mm, "end": v(15.66, -18.67) * mm});
            skLineSegment(sketch, "E164.MirrorCS", {"start": v(20.9, -3.47) * mm, "end": v(23.33, -3.47) * mm});
            skPoint(sketch, "E165.MirrorP", {"position": v(3.82, 0) * mm});
            skPoint(sketch, "E166.MirrorP", {"position": v(27, 0) * mm});
            skArc(sketch, "E167.MirrorCS", {"start": v(15.38, -20.86) * mm, "mid": v(10.66, -23.33) * mm, "end": v(5.44, -24.47) * mm});
            skArc(sketch, "E168.MirrorCS", {"start": v(21.2, -15.03) * mm, "mid": v(23.69, -10.3) * mm, "end": v(24.83, -5.1) * mm});
            skArc(sketch, "E169.MirrorCS", {"start": v(16.89, -11.75) * mm, "mid": v(18.6, -8.45) * mm, "end": v(19.4, -4.83) * mm});
            skArc(sketch, "E170.MirrorCS", {"start": v(16.89, 11.75) * mm, "mid": v(18.6, 8.45) * mm, "end": v(19.4, 4.83) * mm});
            skArc(sketch, "E171.MirrorCS", {"start": v(21.2, 15.03) * mm, "mid": v(23.69, 10.3) * mm, "end": v(24.83, 5.1) * mm});
            skArc(sketch, "E172.MirrorCS", {"start": v(15.38, 20.86) * mm, "mid": v(10.66, 23.33) * mm, "end": v(5.44, 24.47) * mm});
            skArc(sketch, "E173.MirrorCS", {"start": v(12.1, 16.54) * mm, "mid": v(8.8, 18.24) * mm, "end": v(5.18, 19.05) * mm});
            skArc(sketch, "E174.MirrorCS", {"start": v(13.17, -15.7) * mm, "mid": v(14.87, -14.12) * mm, "end": v(16.4, -12.37) * mm, "construction": true});
            skArc(sketch, "E175.MirrorCS", {"start": v(13.17, 15.7) * mm, "mid": v(14.87, 14.12) * mm, "end": v(16.4, 12.37) * mm, "construction": true});
            skArc(sketch, "E176.MirrorCS", {"start": v(12.1, -16.54) * mm, "mid": v(8.8, -18.24) * mm, "end": v(5.18, -19.05) * mm});
            skSolve(sketch);
        }
        {
            var Q0;
            Q0=makeQuery(id+"F12.imprint","IMPRINT",FACE,{"disambiguationData":[TD([[makeQuery(id+"F12.imprint","IMPRINT",EDGE,{"derivedFrom":sQuery(id+"F12.wireOp",EDGE,"E104")}),-1.0]])]});
            var Q1;
            Q1=makeQuery(id+"F12.imprint","IMPRINT",FACE,{"disambiguationData":[TD([[makeQuery(id+"F12.imprint","IMPRINT",EDGE,{"derivedFrom":sQuery(id+"F12.wireOp",EDGE,"E114.MirrorCS")}),1.0]])]});
            var Q2;
            Q2=makeQuery(id+"F12.imprint","IMPRINT",FACE,{"disambiguationData":[TD([[makeQuery(id+"F12.imprint","IMPRINT",EDGE,{"derivedFrom":sQuery(id+"F12.wireOp",EDGE,"E123.MirrorCS")}),1.0]])]});
            var Q3;
            Q3=makeQuery(id+"F12.imprint","IMPRINT",FACE,{"disambiguationData":[TD([[makeQuery(id+"F12.imprint","IMPRINT",EDGE,{"derivedFrom":sQuery(id+"F12.wireOp",EDGE,"E126.MirrorCS")}),1.0]])]});
            var Q4;
            Q4=makeQuery(id+"F12.imprint","IMPRINT",FACE,{"disambiguationData":[TD([[makeQuery(id+"F12.imprint","IMPRINT",EDGE,{"derivedFrom":sQuery(id+"F12.wireOp",EDGE,"E142.MirrorCS")}),1.0]])]});
            var Q5;
            Q5=makeQuery(id+"F12.imprint","IMPRINT",FACE,{"disambiguationData":[TD([[makeQuery(id+"F12.imprint","IMPRINT",EDGE,{"derivedFrom":sQuery(id+"F12.wireOp",EDGE,"E144.MirrorCS")}),-1.0]])]});
            var Q6;
            Q6=makeQuery(id+"F12.imprint","IMPRINT",FACE,{"disambiguationData":[TD([[makeQuery(id+"F12.imprint","IMPRINT",EDGE,{"derivedFrom":sQuery(id+"F12.wireOp",EDGE,"E143.MirrorCS")}),1.0]])]});
            var Q7;
            Q7=makeQuery(id+"F12.imprint","IMPRINT",FACE,{"disambiguationData":[TD([[makeQuery(id+"F12.imprint","IMPRINT",EDGE,{"derivedFrom":sQuery(id+"F12.wireOp",EDGE,"E141.MirrorCS")}),-1.0]])]});
            extrude(context, id + "F13", {"entities" : qUnion([Q0, Q1, Q2, Q3, Q4, Q5, Q6, Q7]), "operationType" : NewBodyOperationType.REMOVE, "oppositeDirection" : true, "depth" : 3 * mm, "offsetDistance" : 25 * mm});
        }
    });
